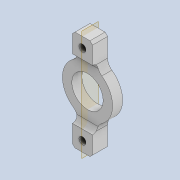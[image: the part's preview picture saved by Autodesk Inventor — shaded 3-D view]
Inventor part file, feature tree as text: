
AUTODESK INVENTOR PART (.ipt)
format: ipt  version: 2020 (Build 240168000, 168)  size: 168,960 bytes
history: native  units: mm
features: other x3, extrude x2, fillet x2, sketch x2, plane x1, chamfer x1, thicken_offset x1, reference x1, projected_geometry x1
ambient origin geometry x8: Origin, YZ Plane, XZ Plane, XY Plane, X Axis, Y Axis, Z Axis, Center Point
bodies: Solid1 (feature_tree)
feature tree (14):
  extrude  "Extrusion1"  Depth=10.0mm
  extrude  "Extrusion2"  Depth=1.0mm
  plane  "Work Plane1"
  chamfer  "Chamfer1"  Distance=8.0mm
  fillet  "Fillet1"  Radius=1.4mm
  fillet  "Fillet2"  Radius=4.0mm
  thicken_offset  "Thicken1"
  sketch  "Sketch1"  dims[d0=6.0mm d1=10.0mm]
  reference  "Reference1"
  sketch  "Sketch2"  dims[d2=8.0mm d3=1.4mm d4=8.0mm d5=1.4mm d6=4.0mm d7=20.0mm d8=2.0mm d9=0.0mm d10=4.0mm d11=4.0mm d12=1.0mm d13=0.0mm d14=0.5mm d15=2.0mm d16=45.0deg d17=2.0mm d18=1.0mm d19=0.12mm d20=0.12mm]
  projected_geometry  "Projected Loop1"
  parser-record x1  (decoder bookkeeping rows leaked as tree rows — omitted from the tree; the rows remain in map.json)
  other  "tip_3_ass.iam"
  other  "bearing_3_6_2:2"
note: 1 file-system path scrubbed to <path> (originals preserved in map.json)
